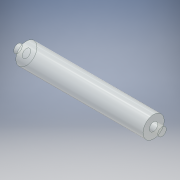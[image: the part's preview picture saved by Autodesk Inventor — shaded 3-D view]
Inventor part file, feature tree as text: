
AUTODESK INVENTOR PART (.ipt)
format: ipt  version: 2017 SP1 (Build 210196100, 196)  size: 112,128 bytes
history: native  units: mm
features: extrude x5, sketch x5
ambient origin geometry x8: Origin, YZ Plane, XZ Plane, XY Plane, X Axis, Y Axis, Z Axis, Center Point
bodies: Solid1 (feature_tree)
feature tree (10):
  extrude  "Extrusion1"  Depth=170.0mm TaperAngle=0.0deg
  extrude  "Extrusion2"  Depth=10.0mm TaperAngle=0.0deg
  extrude  "Extrusion3"  Depth=10.0mm TaperAngle=0.0deg
  extrude  "Extrusion4"  Depth=10.0mm TaperAngle=0.0deg
  extrude  "Extrusion5"  [1 undecoded]
  sketch  "Sketch1"  dims[d0=25.0mm d1=170.0mm d2=0.0mm]
  sketch  "Sketch2"  dims[d3=25.0mm d4=10.0mm d5=0.0mm]
  sketch  "Sketch3"  dims[d6=10.0mm d7=10.0mm d8=0.0mm]
  sketch  "Sketch4"  dims[d9=25.0mm d10=10.0mm d11=0.0mm]
  sketch  "Sketch5"  dims[d12=10.0mm d13=0.0mm]
note: 1 required parameter value undecoded (feature->parameter linkage not recoverable at this tier; creation-order binding heuristic only, values carry confidence <= 0.55)
